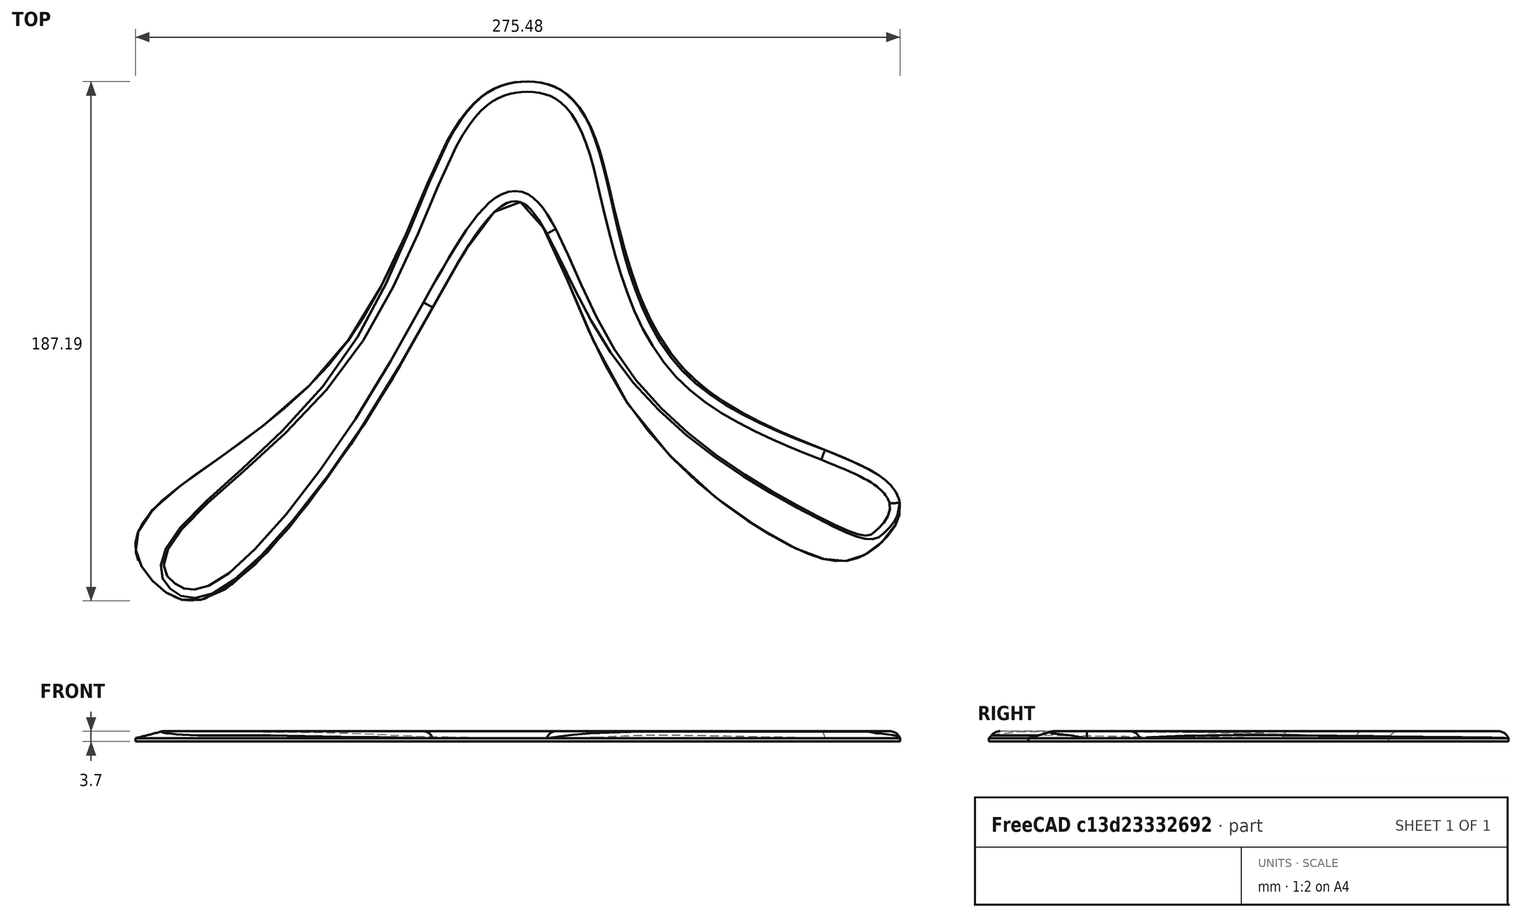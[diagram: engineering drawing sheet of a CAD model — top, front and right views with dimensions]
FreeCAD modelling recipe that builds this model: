
FCSTD DOCUMENT  (FreeCAD 0.20R26720 (Git))
Label: splinebased-3
License: All rights reserved
LicenseURL: http://en.wikipedia.org/wiki/All_rights_reserved
objects: Sketcher::SketchObject×2, PartDesign::Plane×1, PartDesign::AdditiveLoft×1, PartDesign::Pad×1, PartDesign::Fillet×1, PartDesign::Body×1, Mesh::Feature×1
note: 10 computed .brp shape members not serialized (recipe doc carries the construction recipe); baked Part::Feature solids carry a one-line shape summary decoded from their .brp

FEATURE [Sketcher::SketchObject] Sketch  label="Outline"
  FullyConstrained = false
  MapMode = 5
  Support = -> [XY_Plane]
  sketch-geometry (32):
    g0: LineSegment StartX=0 StartY=0 StartZ=0 EndX=-114.715 EndY=-163.83 EndZ=0
    g1: LineSegment StartX=0 StartY=0 StartZ=0 EndX=103.244 EndY=-147.447 EndZ=0
    g2-g15: Circle x14 (B-spline internal-alignment scaffolding for g16; pole/knot coordinates omitted)
    g16: BSplineCurve PolesCount=14 KnotsCount=15 Degree=3 IsPeriodic=1
    g17-g31: GeomPoint x15 (B-spline internal-alignment scaffolding for g16; pole/knot coordinates omitted)
  constraints (13):
    c: Coincident(g0,g-1)
    c: Coincident(g1,g-1)
    c: Distance(g0) = 200
    c: Distance(g1) = 180
    c: Angle(g0,g1) = 1.22173
    c: Angle(g-2,g0) = 2.53073
    c: PointOnObject(g2,g-2)
    c: Weight(g2) = 1
    c: Equal(g2, g3-g9) x7
    c: PointOnObject(g9,g-2)
    c: Equal(g2, g10-g15) x6
    c: InternalAlignment(g2-g15 -> g16) x14
    c: InternalAlignment(g17-g31 -> g16) x15
FEATURE [PartDesign::Plane] DatumPlane  label="Top Plane"
  AttachmentOffset = pos=(0,0,2.5) rot=(0,0,1;0rad)
  Length = 60
  MapMode = 2
  Placement = pos=(0,0,2.5) rot=(0,0,1;0rad)
  ResizeMode = 0
  Support = -> [Sketch]
  Width = 60
FEATURE [Sketcher::SketchObject] Sketch001  label="Top Outline"
  FullyConstrained = false
  MapMode = 5
  Placement = pos=(0,0,2.5) rot=(0,0,1;0rad)
  Support = -> [DatumPlane]
  sketch-geometry (30):
    g0-g13: Circle x14 (B-spline internal-alignment scaffolding for g14; pole/knot coordinates omitted)
    g14: BSplineCurve PolesCount=14 KnotsCount=15 Degree=3 IsPeriodic=1
    g15-g29: GeomPoint x15 (B-spline internal-alignment scaffolding for g14; pole/knot coordinates omitted)
  constraints (4):
    c: Weight(g0) = 1
    c: Equal(g0, g1-g13) x13
    c: InternalAlignment(g0-g13 -> g14) x14
    c: InternalAlignment(g15-g29 -> g14) x15
FEATURE [PartDesign::AdditiveLoft] AdditiveLoft  label="Boomerang Loft"
  Closed = true
  Profile = -> Sketch
  Ruled = true
  Sections = -> [Sketch001]
FEATURE [PartDesign::Pad] Pad  label="Bottom Pad"
  BaseFeature = -> AdditiveLoft
  Direction = (0,0,-1)
  Length = 1.2
  Length2 = 100
  Profile = -> AdditiveLoft [Face1]
  Type = 0
FEATURE [PartDesign::Fillet] Fillet  label="Airfoil Fillet"
  Base = -> Pad [Face4]
  BaseFeature = -> Pad
  Radius = 4
  SupportTransform = false
FEATURE [PartDesign::Body] Body  label="Boomerang"
  Group = -> [Sketch,DatumPlane,Sketch001,AdditiveLoft,Pad,Fillet]
  Origin = -> Origin
  Tip = -> Fillet
FEATURE [Mesh::Feature] Mesh  label="Boomerang (Meshed)"
